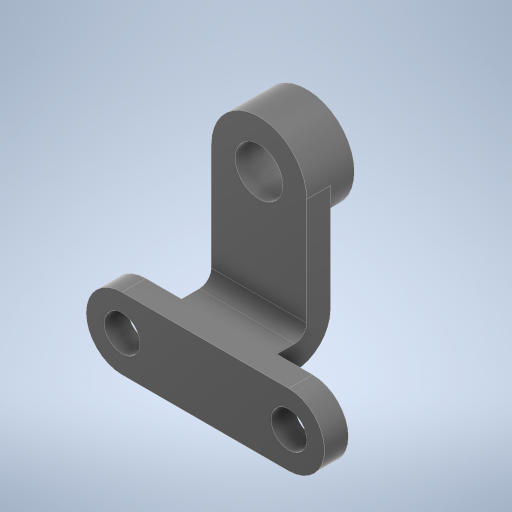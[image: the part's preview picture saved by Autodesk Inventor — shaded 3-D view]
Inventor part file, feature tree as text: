
AUTODESK INVENTOR PART (.ipt)
format: ipt  version: 2024 (Build 280153000, 153)  size: 291,840 bytes
history: native  units: in
note: dims shown in document units (in); Inventor stores cm internally (conversion verified against a paired STEP export)
features: extrude x4, other x2, sketch x1
ambient origin geometry x8: Origin, YZ Plane, XZ Plane, XY Plane, X Axis, Y Axis, Z Axis, Center Point
bodies: Solid1 (feature_tree)
feature tree (7):
  extrude  "SLOT EXT"  Depth=3.5in
  extrude  "J JOINT"  Depth=1.5in
  other  "TOP JOINT"
  extrude  "TOP CYLINDER"  Depth=1.5in
  extrude  "TOP HOLE"  Depth=1.5in
  other  "SLOT SK"
  sketch  "Sketch2"  dims[d0=7.0in d1=3.5in d2=1.5in d3=1.5in d4=1.5in d5=1.0in d6=0.0in d7=0.5in d8=1.5in d9=5.0in d10=2.25in d11=1.0in d12=1.0in d13=4.0in d14=0.0in d15=2.0in d16=2.0in d17=0.0in d18=4.0in d19=0.0in]
